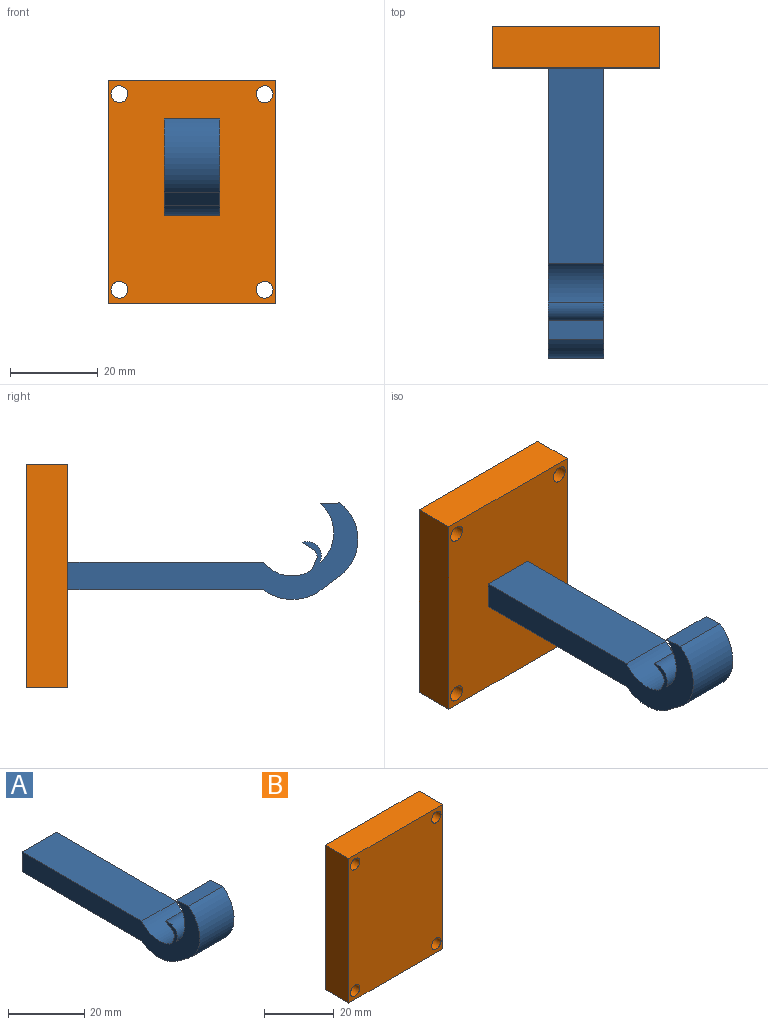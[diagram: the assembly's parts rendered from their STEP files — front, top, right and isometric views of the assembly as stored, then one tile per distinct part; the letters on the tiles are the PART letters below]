
ASSEMBLY  parts=2 mates=1
PART A: 15 faces, bbox 12.7x65.9x22 mm
  f0: plane 44.45x12.7mm, normal (0,0,1), area 564.5mm2, adj f1,f12,f13,f14
  f1: cylinder r=8.11mm len=12.7mm, axis (-1,0,0), area 156.3mm2, adj f0,f2,f13,f14
  f2: plane 12.7x3.08mm, normal (0,0.93,0.37), area 42.1mm2, adj f1,f3,f13,f14
  f3: plane 12.7x1.32mm, normal (0,0.91,-0.42), area 18.5mm2, adj f2,f4,f13,f14
  f4: plane 12.7x2.81mm, normal (0,0.54,-0.84), area 42.6mm2, adj f3,f5,f13,f14
  f5: cylinder r=3.29mm len=12.7mm, axis (-1,0,0), area 96.4mm2, adj f4,f6,f13,f14
  f6: cylinder r=8.59mm len=13.23mm, axis (-1,0,0), area 191.7mm2, adj f5,f7,f13,f14
  f7: plane 12.7x4.46mm, normal (0,0.05,1), area 56.6mm2, adj f6,f8,f13,f14
  f8: cylinder r=10.37mm len=16.61mm, axis (-1,0,0), area 244.6mm2, adj f7,f9,f13,f14
  f9: plane 12.7x4.24mm, normal (0,-0.6,-0.8), area 67.3mm2, adj f8,f10,f13,f14
  f10: cylinder r=10.92mm len=13.08mm, axis (-1,0,0), area 178.2mm2, adj f9,f11,f13,f14
  f11: plane 44.45x12.7mm, normal (0,0,-1), area 564.5mm2, adj f10,f12,f13,f14
  f12: plane 12.7x6.35mm, normal (0,1,0), area 80.6mm2, adj f0,f11,f13,f14
  f13: plane 65.94x21.96mm, normal (1,0,0), area 463.3mm2, adj f0,f1,f2,f3,f4,f5,f6,f7
  f14: plane 65.94x21.96mm, normal (-1,0,0), area 463.3mm2, adj f0,f1,f2,f3,f4,f5,f6,f7
PART B: 10 faces, bbox 38.1x9.5x50.8 mm
  f0: plane 50.8x9.53mm, normal (-1,0,0), area 483.9mm2, adj f1,f7,f8,f9
  f1: plane 38.1x9.53mm, normal (0,0,-1), area 362.9mm2, adj f0,f2,f8,f9
  f2: plane 50.8x9.53mm, normal (1,0,0), area 483.9mm2, adj f1,f7,f8,f9
  f3: cylinder r=1.91mm len=9.53mm, axis (0,1,0), area 114mm2, adj f8,f9
  f4: cylinder r=1.91mm len=9.53mm, axis (0,1,0), area 114mm2, adj f8,f9
  f5: cylinder r=1.91mm len=9.53mm, axis (0,1,0), area 114mm2, adj f8,f9
  f6: cylinder r=1.91mm len=9.53mm, axis (0,1,0), area 114mm2, adj f8,f9
  f7: plane 38.1x9.53mm, normal (0,0,1), area 362.9mm2, adj f0,f2,f8,f9
  f8: plane 50.8x38.1mm, normal (0,-1,0), area 1889.9mm2, adj f0,f1,f2,f3,f4,f5,f6,f7
  f9: plane 50.8x38.1mm, normal (0,1,0), area 1889.9mm2, adj f0,f1,f2,f3,f4,f5,f6,f7
PLACE A t=(1.92,-27.21,0.39)mm
PLACE B t=(1.92,-0.22,0.39)mm
MATE fastened A.f12 <-> B.f8  axis (0,1,0) through (1.92,-4.99,0.39)mm
